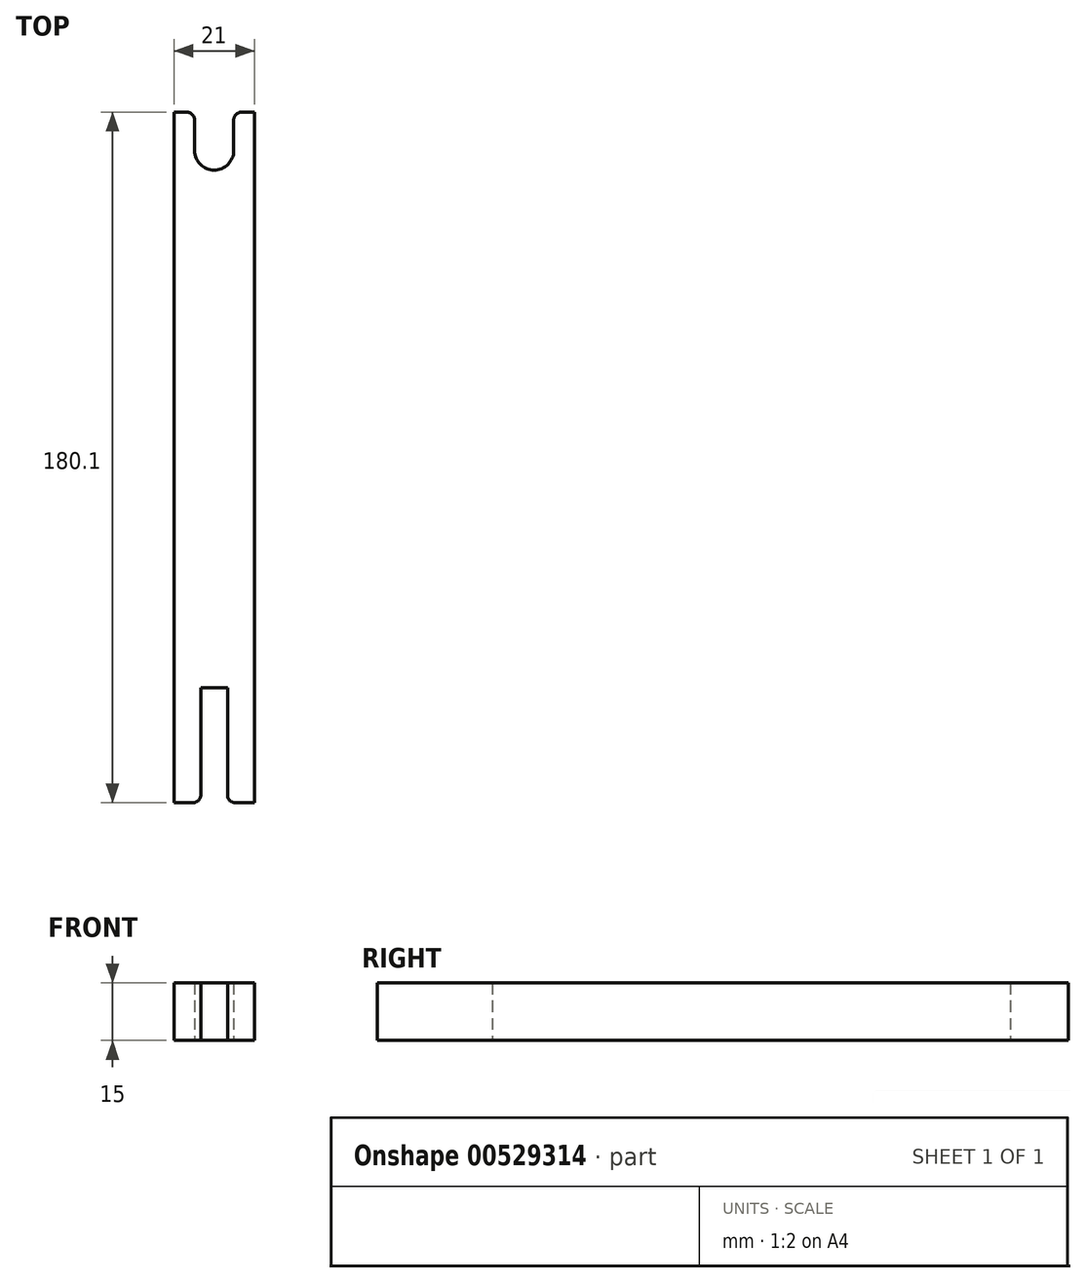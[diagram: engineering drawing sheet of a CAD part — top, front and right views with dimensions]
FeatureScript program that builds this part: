
annotation { "Feature Type Name" : "Feature", "Feature Type Description" : "" }
export const myFeature = defineFeature(function(context is Context, id is Id, definition is map)
    precondition{}
    {
        {
            var Q0;
            Q0=qCreatedBy(makeId("Top.planeOp"),FACE);
            var sketch = newSketch(context, id + "F0", { "sketchPlane" : qUnion([Q0])});
            skLineSegment(sketch, "E0.bottom", {"start": v(10.5, -90.05) * mm, "end": v(-10.5, -90.05) * mm});
            skLineSegment(sketch, "E0.top", {"start": v(10.5, 90.05) * mm, "end": v(-10.5, 90.05) * mm});
            skLineSegment(sketch, "E0.left", {"start": v(10.5, -90.05) * mm, "end": v(10.5, 90.05) * mm});
            skLineSegment(sketch, "E0.right", {"start": v(-10.5, -90.05) * mm, "end": v(-10.5, 90.05) * mm});
            skPoint(sketch, "E0.middle", {"position": v(0, 0) * mm});
            skLineSegment(sketch, "E1.bottom", {"start": v(3.5, -60.05) * mm, "end": v(-3.5, -60.05) * mm});
            skLineSegment(sketch, "E1.top", {"start": v(3.5, -120.05) * mm, "end": v(-3.5, -120.05) * mm});
            skLineSegment(sketch, "E1.left", {"start": v(3.5, -60.05) * mm, "end": v(3.5, -120.05) * mm});
            skLineSegment(sketch, "E1.right", {"start": v(-3.5, -60.05) * mm, "end": v(-3.5, -120.05) * mm});
            skPoint(sketch, "E1.middle", {"position": v(0, -90.05) * mm});
            skPoint(sketch, "E2", {"position": v(0, 90.05) * mm});
            skLineSegment(sketch, "E3.bottom", {"start": v(5.1, 80.05) * mm, "end": v(-5.1, 80.05) * mm});
            skLineSegment(sketch, "E3.top", {"start": v(5.1, 100.05) * mm, "end": v(-5.1, 100.05) * mm});
            skLineSegment(sketch, "E3.left", {"start": v(5.1, 80.05) * mm, "end": v(5.1, 100.05) * mm});
            skLineSegment(sketch, "E3.right", {"start": v(-5.1, 80.05) * mm, "end": v(-5.1, 100.05) * mm});
            skArc(sketch, "E4", {"start": v(-5.1, 80.05) * mm, "mid": v(0, 74.95) * mm, "end": v(5.1, 80.05) * mm});
            skSolve(sketch);
        }
        {
            var Q0;
            {var subQ7=sQuery(id+"F0.wireOp",EDGE,"E0.left");Q0=makeQuery(id+"F0.imprint","IMPRINT",FACE,{"disambiguationData":[TD([[makeQuery(id+"F0.imprint","IMPRINT",EDGE,{"derivedFrom":subQ7}),1.0]])]});}
            extrude(context, id + "F1", {"entities" : qUnion([Q0]), "endBound" : BoundingType.SYMMETRIC, "depth" : 15 * mm, "offsetDistance" : 25 * mm});
        }
        {
            var Q0;
            Q0=makeQuery(id+"F1.opExtrude","SWEPT_EDGE",EDGE,{"disambiguationData":[OSD([sQuery(id+"F0.wireOp",EDGE,"E0.top"),sQuery(id+"F0.wireOp",EDGE,"E3.left")])]});
            var Q1;
            Q1=makeQuery(id+"F1.opExtrude","SWEPT_EDGE",EDGE,{"disambiguationData":[OSD([sQuery(id+"F0.wireOp",EDGE,"E0.top"),sQuery(id+"F0.wireOp",EDGE,"E3.right")])]});
            var Q2;
            Q2=makeQuery(id+"F1.opExtrude","SWEPT_EDGE",EDGE,{"disambiguationData":[OSD([sQuery(id+"F0.wireOp",EDGE,"E0.bottom"),sQuery(id+"F0.wireOp",EDGE,"E1.right")])]});
            var Q3;
            Q3=makeQuery(id+"F1.opExtrude","SWEPT_EDGE",EDGE,{"disambiguationData":[OSD([sQuery(id+"F0.wireOp",EDGE,"E0.bottom"),sQuery(id+"F0.wireOp",EDGE,"E1.left")])]});
            fillet(context, id + "F2", {"entities" : qUnion([Q0, Q1, Q2, Q3]), "radius" : 2 * mm, "tangentPropagation" : true, "allowEdgeOverflow" : false});
        }
    });
